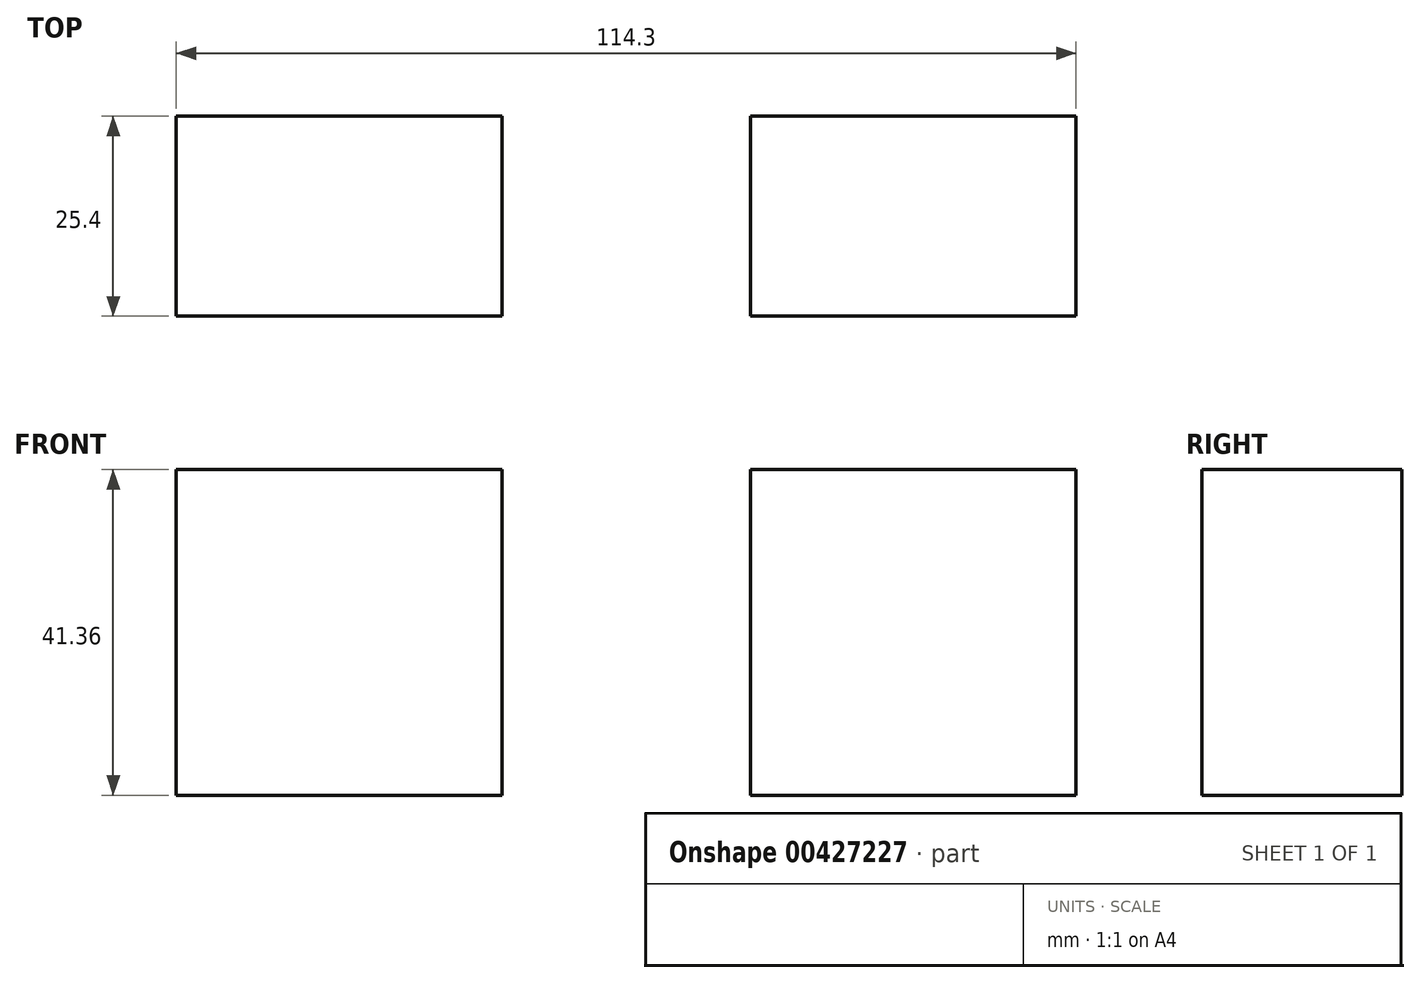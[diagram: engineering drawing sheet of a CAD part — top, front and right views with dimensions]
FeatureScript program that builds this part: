
annotation { "Feature Type Name" : "Feature", "Feature Type Description" : "" }
export const myFeature = defineFeature(function(context is Context, id is Id, definition is map)
    precondition{}
    {
        {
            var Q0;
            Q0=qCreatedBy(makeId("Front.planeOp"),FACE);
            var sketch = newSketch(context, id + "F0", { "sketchPlane" : qUnion([Q0])});
            skLineSegment(sketch, "E0.bottom", {"start": v(-15.78, 28.85) * mm, "end": v(-57.15, 28.85) * mm});
            skLineSegment(sketch, "E0.top", {"start": v(-15.78, 70.21) * mm, "end": v(-57.15, 70.21) * mm});
            skLineSegment(sketch, "E0.left", {"start": v(-15.78, 28.85) * mm, "end": v(-15.78, 70.21) * mm});
            skLineSegment(sketch, "E0.right", {"start": v(-57.15, 28.85) * mm, "end": v(-57.15, 70.21) * mm});
            skPoint(sketch, "E0.middle", {"position": v(-36.47, 49.53) * mm});
            skSolve(sketch);
        }
        {
            var Q0;
            Q0=makeQuery(id+"F0.imprint","IMPRINT",FACE,{"disambiguationData":[TD([[makeQuery(id+"F0.imprint","IMPRINT",EDGE,{"derivedFrom":sQuery(id+"F0.wireOp",EDGE,"E0.bottom")}),-1.0]])]});
            extrude(context, id + "F1", {"entities" : qUnion([Q0]), "endBound" : BoundingType.SYMMETRIC, "depth" : 25.4 * mm});
        }
        {
            var Q0;
            Q0=makeQuery(id+"F1.opExtrude","SWEPT_BODY",BODY,{"disambiguationData":[OSD([sQuery(id+"F0.wireOp",EDGE,"E0.bottom"),sQuery(id+"F0.wireOp",EDGE,"E0.top"),sQuery(id+"F0.wireOp",EDGE,"E0.left"),sQuery(id+"F0.wireOp",EDGE,"E0.right")])]});
            var Q1;
            Q1=qCreatedBy(makeId("Right.planeOp"),FACE);
            mirror(context, id + "F2", {"entities" : qUnion([Q0]), "mirrorPlane" : qUnion([Q1])});
        }
    });
